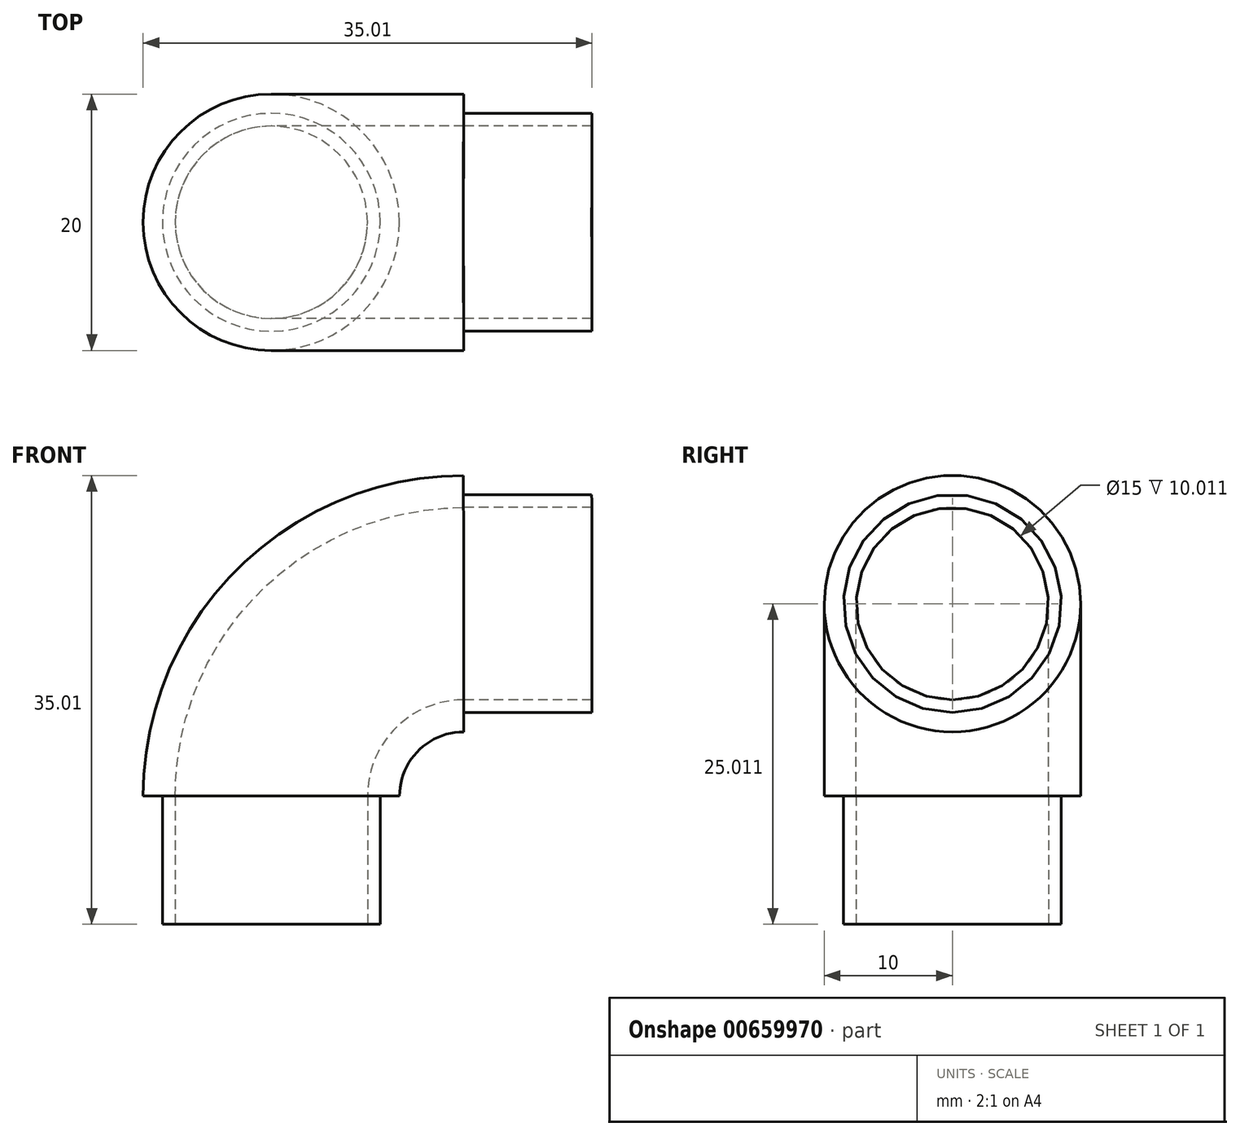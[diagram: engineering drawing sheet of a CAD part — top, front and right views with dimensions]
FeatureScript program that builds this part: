
annotation { "Feature Type Name" : "Feature", "Feature Type Description" : "" }
export const myFeature = defineFeature(function(context is Context, id is Id, definition is map)
    precondition{}
    {
        {
            var Q0;
            Q0=qCreatedBy(makeId("Top.planeOp"),FACE);
            var sketch = newSketch(context, id + "F0", { "sketchPlane" : qUnion([Q0])});
            skCircle(sketch, "E0", {"center": v(0, 0) * mm, "radius": 7.5 * mm});
            skSolve(sketch);
        }
        {
            var Q0;
            Q0=makeQuery(id+"F0.imprint","IMPRINT",FACE,{"disambiguationData":[TD([[makeQuery(id+"F0.imprint","IMPRINT",EDGE,{"derivedFrom":sQuery(id+"F0.wireOp",EDGE,"E0")}),1.0]])]});
            var sketch = newSketch(context, id + "F1", { "sketchPlane" : qUnion([Q0])});
            skLineSegment(sketch, "E1", {"start": v(0, 0) * mm, "end": v(15, 0) * mm});
            skSolve(sketch);
        }
        {
            var Q0;
            Q0=qCreatedBy(makeId("Front.planeOp"),FACE);
            var sketch = newSketch(context, id + "F2", { "sketchPlane" : qUnion([Q0])});
            skLineSegment(sketch, "E2", {"start": v(15, 0) * mm, "end": v(15, 15.01) * mm});
            skLineSegment(sketch, "E3", {"start": v(15, 15.01) * mm, "end": v(25, 15.01) * mm});
            skSolve(sketch);
        }
        {
            var Q0;
            Q0=qCreatedBy(makeId("Front.planeOp"),FACE);
            var sketch = newSketch(context, id + "F3", { "sketchPlane" : qUnion([Q0])});
            skArc(sketch, "E4", {"start": v(0, 0) * mm, "mid": v(4.4, 10.61) * mm, "end": v(15, 15.01) * mm});
            skSolve(sketch);
        }
        {
            var Q0;
            Q0=makeQuery(id+"F0.imprint","IMPRINT",FACE,{"disambiguationData":[TD([[makeQuery(id+"F0.imprint","IMPRINT",EDGE,{"derivedFrom":sQuery(id+"F0.wireOp",EDGE,"E0")}),1.0]])]});
            var Q1;
            Q1=sQuery(id+"F3.wireOp",EDGE,"E4");
            sweep(context, id + "F4", {"profiles" : qUnion([Q0]), "path" : qUnion([Q1])});
        }
        {
            var Q0;
            Q0=makeQuery(id+"F4.opSweep","CAP_FACE",FACE,{"disambiguationData":[OSD([sQuery(id+"F0.wireOp",EDGE,"E0"),sQuery(id+"F3.wireOp",VERTEX,"E4.end")])],"isStart":false});
            var sketch = newSketch(context, id + "F5", { "sketchPlane" : qUnion([Q0])});
            skCircle(sketch, "E5", {"center": v(0, 15) * mm, "radius": 10 * mm});
            skSolve(sketch);
        }
        {
            var Q0;
            Q0=makeQuery(id+"F5.imprint","IMPRINT",FACE,{"disambiguationData":[TD([[makeQuery(id+"F5.imprint","IMPRINT",EDGE,{"derivedFrom":sQuery(id+"F5.wireOp",EDGE,"E5")}),1.0]])]});
            var Q1;
            Q1 = qConstructionFilter(qBodyType(qCreatedBy(id + "F3" ,EDGE), BodyType.WIRE), ConstructionObject.NO);
            sweep(context, id + "F6", {"profiles" : qUnion([Q0]), "path" : qUnion([Q1])});
        }
        {
            var Q0;
            Q0=makeQuery(id+"F4.opSweep","SWEPT_BODY",BODY,{"disambiguationData":[OSD([sQuery(id+"F0.wireOp",EDGE,"E0"),sQuery(id+"F3.wireOp",EDGE,"E4")])]});
            var Q1;
            Q1=makeQuery(id+"F6.opSweep","SWEPT_BODY",BODY,{"disambiguationData":[OSD([sQuery(id+"F0.wireOp",EDGE,"E0"),sQuery(id+"F3.wireOp",VERTEX,"E4.end"),sQuery(id+"F3.wireOp",EDGE,"E4"),sQuery(id+"F5.wireOp",EDGE,"E5")])]});
            booleanBodies(context, id + "F7", {"operationType" : BooleanOperationType.SUBTRACTION, "tools" : qUnion([Q0]), "targets" : qUnion([Q1])});
        }
        {
            var Q0;
            Q0=makeQuery(id+"F6.opSweep","CAP_FACE",FACE,{"disambiguationData":[OSD([sQuery(id+"F0.wireOp",EDGE,"E0"),sQuery(id+"F3.wireOp",VERTEX,"E4.start"),sQuery(id+"F3.wireOp",VERTEX,"E4.end"),sQuery(id+"F5.wireOp",EDGE,"E5")])],"isStart":false});
            var sketch = newSketch(context, id + "F8", { "sketchPlane" : qUnion([Q0])});
            skCircle(sketch, "E6", {"center": v(0, 0) * mm, "radius": 8.5 * mm});
            skSolve(sketch);
        }
        {
            var Q0;
            Q0=qCreatedBy(makeId("Front.planeOp"),FACE);
            var sketch = newSketch(context, id + "F9", { "sketchPlane" : qUnion([Q0])});
            skLineSegment(sketch, "E7", {"start": v(0, 0) * mm, "end": v(0, -10) * mm});
            skSolve(sketch);
        }
        {
            var Q0;
            Q0=makeQuery(id+"F8.imprint","IMPRINT",FACE,{"disambiguationData":[TD([[makeQuery(id+"F8.imprint","IMPRINT",EDGE,{"derivedFrom":sQuery(id+"F8.wireOp",EDGE,"E6")}),1.0]])]});
            var Q1;
            Q1=sQuery(id+"F9.wireOp",EDGE,"E7");
            sweep(context, id + "F10", {"operationType" : NewBodyOperationType.ADD, "profiles" : qUnion([Q0]), "path" : qUnion([Q1])});
        }
        {
            var Q0;
            Q0=makeQuery(id+"F6.opSweep","CAP_FACE",FACE,{"disambiguationData":[OSD([sQuery(id+"F0.wireOp",EDGE,"E0"),sQuery(id+"F3.wireOp",VERTEX,"E4.end"),sQuery(id+"F5.wireOp",EDGE,"E5")])],"isStart":true});
            var sketch = newSketch(context, id + "F11", { "sketchPlane" : qUnion([Q0])});
            skCircle(sketch, "E8", {"center": v(0, 15) * mm, "radius": 8.5 * mm});
            skSolve(sketch);
        }
        {
            var Q0;
            Q0=makeQuery(id+"F11.imprint","IMPRINT",FACE,{"disambiguationData":[TD([[makeQuery(id+"F11.imprint","IMPRINT",EDGE,{"derivedFrom":sQuery(id+"F11.wireOp",EDGE,"E8")}),1.0]])]});
            var Q1;
            Q1=sQuery(id+"F11.wireOp",EDGE,"E8");
            var Q2;
            Q2=makeQuery(id+"F6.opSweep","CAP_EDGE",EDGE,{"disambiguationData":[OSD([sQuery(id+"F0.wireOp",EDGE,"E0"),sQuery(id+"F3.wireOp",VERTEX,"E4.end")])],"isStart":true});
            var Q3;
            Q3=sQuery(id+"F2.wireOp",EDGE,"E3");
            sweep(context, id + "F12", {"operationType" : NewBodyOperationType.ADD, "profiles" : qUnion([Q0]), "surfaceProfiles" : qUnion([Q1, Q2]), "path" : qUnion([Q3])});
        }
    });
